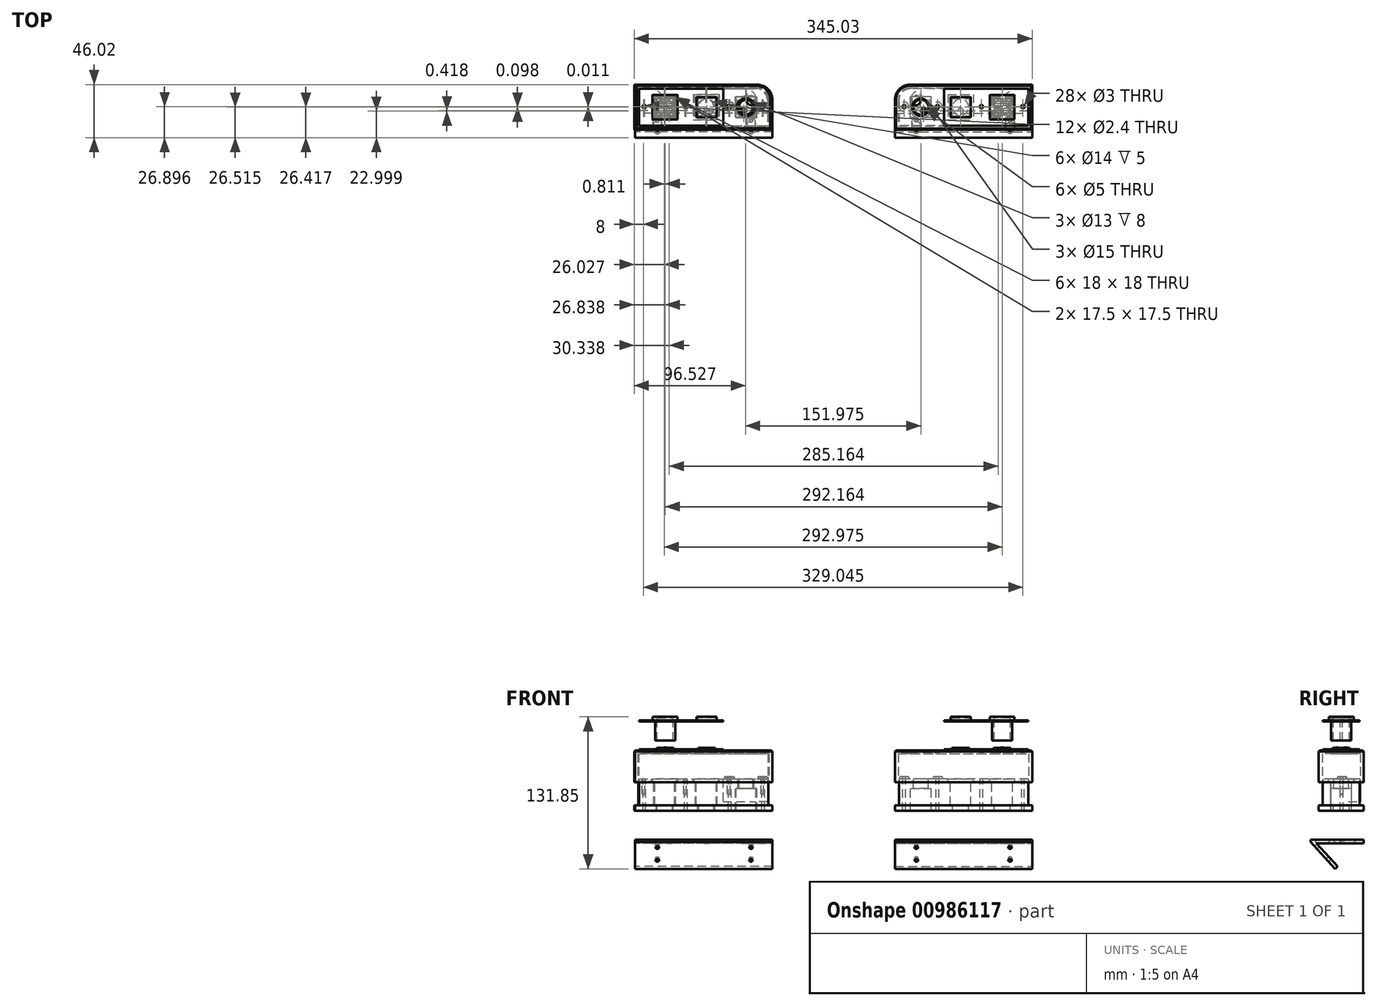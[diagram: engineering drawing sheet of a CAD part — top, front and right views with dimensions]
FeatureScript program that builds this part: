
annotation { "Feature Type Name" : "Feature", "Feature Type Description" : "" }
export const myFeature = defineFeature(function(context is Context, id is Id, definition is map)
    precondition{}
    {
        {
            var Q0;
            Q0=qCreatedBy(makeId("Top.planeOp"),FACE);
            var sketch = newSketch(context, id + "F0", { "sketchPlane" : qUnion([Q0])});
            skLineSegment(sketch, "E0.bottom", {"start": v(66.11, 78.9) * mm, "end": v(169.11, 78.9) * mm});
            skLineSegment(sketch, "E0.top", {"start": v(56.11, 45.9) * mm, "end": v(169.11, 45.9) * mm});
            skLineSegment(sketch, "E0.left", {"start": v(56.11, 68.9) * mm, "end": v(56.11, 45.9) * mm});
            skLineSegment(sketch, "E0.right", {"start": v(169.11, 78.9) * mm, "end": v(169.11, 45.9) * mm});
            skLineSegment(sketch, "E1.bottom", {"start": v(-169.92, 79) * mm, "end": v(-66.92, 79) * mm});
            skLineSegment(sketch, "E1.top", {"start": v(-169.92, 46) * mm, "end": v(-56.92, 46) * mm});
            skLineSegment(sketch, "E1.left", {"start": v(-169.92, 79) * mm, "end": v(-169.92, 46) * mm});
            skLineSegment(sketch, "E1.right", {"start": v(-56.92, 69) * mm, "end": v(-56.92, 46) * mm});
            skPoint(sketch, "E2.visualSharp", {"position": v(-56.92, 79) * mm});
            skArc(sketch, "E2.filletArc", {"start": v(-56.92, 69) * mm, "mid": v(-59.85, 76.07) * mm, "end": v(-66.92, 79) * mm});
            skPoint(sketch, "E3.visualSharp", {"position": v(56.11, 78.9) * mm});
            skArc(sketch, "E3.filletArc", {"start": v(66.11, 78.9) * mm, "mid": v(59.04, 75.97) * mm, "end": v(56.11, 68.9) * mm});
            skSolve(sketch);
        }
        {
            var Q0;
            Q0=qSketchRegion(id+"F0",true);
            extrude(context, id + "F1", {"entities" : qUnion([Q0]), "depth" : 5 * mm, "hasSecondDirection" : true, "secondDirectionOppositeDirection" : true, "secondDirectionDepth" : 19.6 * mm, "offsetDistance" : 25 * mm});
        }
        {
            var Q0;
            Q0=makeQuery(id+"F1.opExtrude","CAP_FACE",FACE,{"disambiguationData":[OSD([sQuery(id+"F0.wireOp",EDGE,"E0.bottom"),sQuery(id+"F0.wireOp",EDGE,"E0.top"),sQuery(id+"F0.wireOp",EDGE,"E0.left"),sQuery(id+"F0.wireOp",EDGE,"E0.right"),sQuery(id+"F0.wireOp",EDGE,"E3.filletArc")])],"isStart":true});
            var Q1;
            Q1=makeQuery(id+"F1.opExtrude","CAP_FACE",FACE,{"disambiguationData":[OSD([sQuery(id+"F0.wireOp",EDGE,"E1.bottom"),sQuery(id+"F0.wireOp",EDGE,"E1.top"),sQuery(id+"F0.wireOp",EDGE,"E1.left"),sQuery(id+"F0.wireOp",EDGE,"E1.right"),sQuery(id+"F0.wireOp",EDGE,"E2.filletArc")])],"isStart":true});
            shell(context, id + "F2", {"entities" : qUnion([Q0, Q1]), "thickness" : 3 * mm, "oppositeDirection" : true});
        }
        {
            var Q0;
            Q0=makeQuery(id+"F1.opExtrude","CAP_FACE",FACE,{"disambiguationData":[OSD([sQuery(id+"F0.wireOp",EDGE,"E0.bottom"),sQuery(id+"F0.wireOp",EDGE,"E0.top"),sQuery(id+"F0.wireOp",EDGE,"E0.left"),sQuery(id+"F0.wireOp",EDGE,"E0.right"),sQuery(id+"F0.wireOp",EDGE,"E3.filletArc")])],"isStart":false});
            cPlane(context, id + "F3", {"entities" : qUnion([Q0]), "cplaneType" : CPlaneType.OFFSET, "offset" : 25 * mm, "width" : 150 * mm, "height" : 150 * mm});
        }
        {
            var Q0;
            Q0=qCreatedBy(id+"F3.planeOp",FACE);
            var sketch = newSketch(context, id + "F4", { "sketchPlane" : qUnion([Q0])});
            skLineSegment(sketch, "E4.bottom", {"start": v(-155.9, 71.5) * mm, "end": v(-137.9, 71.5) * mm});
            skLineSegment(sketch, "E4.top", {"start": v(-155.9, 53.5) * mm, "end": v(-137.9, 53.5) * mm});
            skLineSegment(sketch, "E4.left", {"start": v(-155.9, 71.5) * mm, "end": v(-155.9, 53.5) * mm});
            skLineSegment(sketch, "E4.right", {"start": v(-137.9, 71.5) * mm, "end": v(-137.9, 53.5) * mm});
            skLineSegment(sketch, "E5.bottom", {"start": v(-119.9, 71.5) * mm, "end": v(-101.9, 71.5) * mm});
            skLineSegment(sketch, "E5.top", {"start": v(-119.9, 53.5) * mm, "end": v(-101.9, 53.5) * mm});
            skLineSegment(sketch, "E5.left", {"start": v(-119.9, 71.5) * mm, "end": v(-119.9, 53.5) * mm});
            skLineSegment(sketch, "E5.right", {"start": v(-101.9, 71.5) * mm, "end": v(-101.9, 53.5) * mm});
            skCircle(sketch, "E6", {"center": v(-76.4, 62.5) * mm, "radius": 7.5 * mm});
            skCircle(sketch, "E7", {"center": v(75.58, 62.4) * mm, "radius": 7.5 * mm});
            skLineSegment(sketch, "E8.bottom", {"start": v(101.08, 71.4) * mm, "end": v(119.08, 71.4) * mm});
            skLineSegment(sketch, "E8.top", {"start": v(101.08, 53.4) * mm, "end": v(119.08, 53.4) * mm});
            skLineSegment(sketch, "E8.left", {"start": v(101.08, 71.4) * mm, "end": v(101.08, 53.4) * mm});
            skLineSegment(sketch, "E8.right", {"start": v(119.08, 71.4) * mm, "end": v(119.08, 53.4) * mm});
            skLineSegment(sketch, "E9.bottom", {"start": v(137.08, 71.4) * mm, "end": v(155.08, 71.4) * mm});
            skLineSegment(sketch, "E9.top", {"start": v(137.08, 53.4) * mm, "end": v(155.08, 53.4) * mm});
            skLineSegment(sketch, "E9.left", {"start": v(137.08, 71.4) * mm, "end": v(137.08, 53.4) * mm});
            skLineSegment(sketch, "E9.right", {"start": v(155.08, 71.4) * mm, "end": v(155.08, 53.4) * mm});
            skSolve(sketch);
        }
        {
            var Q0;
            Q0=qSketchRegion(id+"F4",true);
            extrude(context, id + "F5", {"entities" : qUnion([Q0]), "operationType" : NewBodyOperationType.REMOVE, "oppositeDirection" : true, "depth" : 50 * mm});
        }
        {
            var Q0;
            Q0=makeQuery(id+"F1.opExtrude","CAP_FACE",FACE,{"disambiguationData":[OSD([sQuery(id+"F0.wireOp",EDGE,"E1.bottom"),sQuery(id+"F0.wireOp",EDGE,"E1.top"),sQuery(id+"F0.wireOp",EDGE,"E1.left"),sQuery(id+"F0.wireOp",EDGE,"E1.right"),sQuery(id+"F0.wireOp",EDGE,"E2.filletArc")])],"isStart":false});
            cPlane(context, id + "F6", {"entities" : qUnion([Q0]), "cplaneType" : CPlaneType.OFFSET, "offset" : 0 * mm, "width" : 150 * mm, "height" : 150 * mm});
        }
        {
            var Q0;
            Q0=qCreatedBy(id+"F6.planeOp",FACE);
            var sketch = newSketch(context, id + "F7", { "sketchPlane" : qUnion([Q0])});
            skPoint(sketch, "E10", {"position": v(-164.92, 62.89) * mm});
            skPoint(sketch, "E11", {"position": v(-128.9, 62.89) * mm});
            skPoint(sketch, "E12", {"position": v(-90.9, 62.89) * mm});
            skPoint(sketch, "E13", {"position": v(-61.92, 62.89) * mm});
            skPoint(sketch, "E14", {"position": v(61.11, 62.89) * mm});
            skPoint(sketch, "E15", {"position": v(90.08, 62.89) * mm});
            skPoint(sketch, "E16", {"position": v(128.08, 62.89) * mm});
            skPoint(sketch, "E17", {"position": v(164.11, 62.89) * mm});
            skSolve(sketch);
        }
        {
            var Q0;
            Q0=sQuery(id+"F7.wireOp",VERTEX,"E11");
            var Q1;
            Q1=sQuery(id+"F7.wireOp",VERTEX,"E17");
            var Q2;
            Q2=sQuery(id+"F7.wireOp",VERTEX,"E16");
            var Q3;
            Q3=sQuery(id+"F7.wireOp",VERTEX,"E10");
            var Q4;
            Q4=sQuery(id+"F7.wireOp",VERTEX,"E15");
            var Q5;
            Q5=sQuery(id+"F7.wireOp",VERTEX,"E14");
            var Q6;
            Q6=sQuery(id+"F7.wireOp",VERTEX,"E12");
            var Q7;
            Q7=sQuery(id+"F7.wireOp",VERTEX,"E13");
            var Q8;
            Q8=makeQuery(id+"F1.opExtrude","SWEPT_BODY",BODY,{"disambiguationData":[OSD([sQuery(id+"F0.wireOp",EDGE,"E0.bottom"),sQuery(id+"F0.wireOp",EDGE,"E0.top"),sQuery(id+"F0.wireOp",EDGE,"E0.left"),sQuery(id+"F0.wireOp",EDGE,"E0.right"),sQuery(id+"F0.wireOp",EDGE,"E3.filletArc")])]});
            var Q9;
            Q9=makeQuery(id+"F1.opExtrude","SWEPT_BODY",BODY,{"disambiguationData":[OSD([sQuery(id+"F0.wireOp",EDGE,"E1.bottom"),sQuery(id+"F0.wireOp",EDGE,"E1.top"),sQuery(id+"F0.wireOp",EDGE,"E1.left"),sQuery(id+"F0.wireOp",EDGE,"E1.right"),sQuery(id+"F0.wireOp",EDGE,"E2.filletArc")])]});
            hole(context, id + "F8", {"style" : HoleStyle.SIMPLE, "endStyle" : HoleEndStyle.BLIND, "holeDiameter" : 3 * mm, "holeDepth" : 40 * mm, "startFromSketch" : true, "locations" : qUnion([Q0, Q1, Q2, Q3, Q4, Q5, Q6, Q7]), "scope" : qUnion([Q8, Q9])});
        }
        {
            var Q0;
            Q0=makeQuery(id+"F1.opExtrude","CAP_EDGE",EDGE,{"disambiguationData":[OSD([sQuery(id+"F0.wireOp",EDGE,"E1.top")])],"isStart":false});
            var Q1;
            Q1=makeQuery(id+"F1.opExtrude","CAP_EDGE",EDGE,{"disambiguationData":[OSD([sQuery(id+"F0.wireOp",EDGE,"E1.left")])],"isStart":false});
            var Q2;
            Q2=makeQuery(id+"F1.opExtrude","CAP_EDGE",EDGE,{"disambiguationData":[OSD([sQuery(id+"F0.wireOp",EDGE,"E1.bottom")])],"isStart":false});
            var Q3;
            Q3=makeQuery(id+"F1.opExtrude","CAP_EDGE",EDGE,{"disambiguationData":[OSD([sQuery(id+"F0.wireOp",EDGE,"E0.left")])],"isStart":false});
            var Q4;
            Q4=makeQuery(id+"F1.opExtrude","CAP_EDGE",EDGE,{"disambiguationData":[OSD([sQuery(id+"F0.wireOp",EDGE,"E0.top")])],"isStart":false});
            var Q5;
            Q5=makeQuery(id+"F1.opExtrude","CAP_EDGE",EDGE,{"disambiguationData":[OSD([sQuery(id+"F0.wireOp",EDGE,"E0.right")])],"isStart":false});
            chamfer(context, id + "F9", {"entities" : qUnion([Q0, Q1, Q2, Q3, Q4, Q5]), "width" : 1 * mm, "tangentPropagation" : true});
        }
        {
            var Q0;
            Q0=makeQuery(id+"F1.opExtrude","CAP_FACE",FACE,{"disambiguationData":[OSD([sQuery(id+"F0.wireOp",EDGE,"E0.bottom"),sQuery(id+"F0.wireOp",EDGE,"E0.top"),sQuery(id+"F0.wireOp",EDGE,"E0.left"),sQuery(id+"F0.wireOp",EDGE,"E0.right"),sQuery(id+"F0.wireOp",EDGE,"E3.filletArc")])],"isStart":true});
            cPlane(context, id + "F10", {"entities" : qUnion([Q0]), "cplaneType" : CPlaneType.OFFSET, "offset" : 25 * mm, "width" : 150 * mm, "height" : 150 * mm});
        }
        {
            var Q0;
            Q0=qCreatedBy(id+"F10.planeOp",FACE);
            var sketch = newSketch(context, id + "F11", { "sketchPlane" : qUnion([Q0])});
            skLineSegment(sketch, "E18.bottom", {"start": v(53.11, -42.9) * mm, "end": v(172.11, -42.9) * mm});
            skLineSegment(sketch, "E18.top", {"start": v(66.11, -81.9) * mm, "end": v(172.11, -81.9) * mm});
            skLineSegment(sketch, "E18.left", {"start": v(53.11, -42.9) * mm, "end": v(53.11, -68.9) * mm});
            skLineSegment(sketch, "E18.right", {"start": v(172.11, -42.9) * mm, "end": v(172.11, -81.9) * mm});
            skLineSegment(sketch, "E19.bottom", {"start": v(-172.92, -43) * mm, "end": v(-53.92, -43) * mm});
            skLineSegment(sketch, "E19.top", {"start": v(-172.92, -81.9) * mm, "end": v(-66.92, -81.9) * mm});
            skLineSegment(sketch, "E19.left", {"start": v(-172.92, -43) * mm, "end": v(-172.92, -81.9) * mm});
            skLineSegment(sketch, "E19.right", {"start": v(-53.92, -43) * mm, "end": v(-53.92, -68.9) * mm});
            skPoint(sketch, "E20.visualSharp", {"position": v(53.11, -81.9) * mm});
            skArc(sketch, "E20.filletArc", {"start": v(53.11, -68.9) * mm, "mid": v(56.92, -78.09) * mm, "end": v(66.11, -81.9) * mm});
            skPoint(sketch, "E21.visualSharp", {"position": v(-53.92, -81.9) * mm});
            skArc(sketch, "E21.filletArc", {"start": v(-66.92, -81.9) * mm, "mid": v(-57.73, -78.09) * mm, "end": v(-53.92, -68.9) * mm});
            skSolve(sketch);
        }
        {
            var Q0;
            Q0=qSketchRegion(id+"F11",true);
            extrude(context, id + "F12", {"entities" : qUnion([Q0]), "oppositeDirection" : true, "depth" : 5 * mm, "offsetDistance" : 25 * mm});
        }
        {
            var Q0;
            Q0=makeQuery(id+"F12.opExtrude","CAP_FACE",FACE,{"disambiguationData":[OSD([sQuery(id+"F11.wireOp",EDGE,"E18.bottom"),sQuery(id+"F11.wireOp",EDGE,"E18.top"),sQuery(id+"F11.wireOp",EDGE,"E18.left"),sQuery(id+"F11.wireOp",EDGE,"E18.right"),sQuery(id+"F11.wireOp",EDGE,"E20.filletArc")])],"isStart":false});
            cPlane(context, id + "F13", {"entities" : qUnion([Q0]), "cplaneType" : CPlaneType.OFFSET, "offset" : 25 * mm, "width" : 150 * mm, "height" : 150 * mm});
        }
        {
            var Q0;
            Q0=makeQuery(id+"F12.opExtrude","CAP_FACE",FACE,{"disambiguationData":[OSD([sQuery(id+"F11.wireOp",EDGE,"E18.bottom"),sQuery(id+"F11.wireOp",EDGE,"E18.top"),sQuery(id+"F11.wireOp",EDGE,"E18.left"),sQuery(id+"F11.wireOp",EDGE,"E18.right"),sQuery(id+"F11.wireOp",EDGE,"E20.filletArc")])],"isStart":false});
            cPlane(context, id + "F14", {"entities" : qUnion([Q0]), "cplaneType" : CPlaneType.OFFSET, "offset" : 0 * mm, "width" : 150 * mm, "height" : 150 * mm});
        }
        {
            var Q0;
            Q0=qCreatedBy(id+"F14.planeOp",FACE);
            var sketch = newSketch(context, id + "F15", { "sketchPlane" : qUnion([Q0])});
            skLineSegment(sketch, "E22.bottom", {"start": v(66.61, 78.4) * mm, "end": v(168.61, 78.4) * mm});
            skLineSegment(sketch, "E22.top", {"start": v(56.61, 46.4) * mm, "end": v(168.61, 46.4) * mm});
            skLineSegment(sketch, "E22.left", {"start": v(56.61, 68.4) * mm, "end": v(56.61, 46.4) * mm});
            skLineSegment(sketch, "E22.right", {"start": v(168.61, 78.4) * mm, "end": v(168.61, 46.4) * mm});
            skPoint(sketch, "E23.oppositeSnap0", {"position": v(112.61, 46.4) * mm});
            skPoint(sketch, "E24.visualSharp", {"position": v(56.61, 78.4) * mm});
            skArc(sketch, "E24.filletArc", {"start": v(66.61, 78.4) * mm, "mid": v(59.54, 75.47) * mm, "end": v(56.61, 68.4) * mm});
            skSolve(sketch);
        }
        {
            var Q0;
            Q0=qSketchRegion(id+"F15",true);
            extrude(context, id + "F16", {"entities" : qUnion([Q0]), "operationType" : NewBodyOperationType.ADD, "depth" : 3 * mm, "offsetDistance" : 25 * mm});
        }
        {
            var Q0;
            Q0=qCreatedBy(id+"F14.planeOp",FACE);
            var sketch = newSketch(context, id + "F17", { "sketchPlane" : qUnion([Q0])});
            skLineSegment(sketch, "E25.bottom", {"start": v(-169.42, 78.5) * mm, "end": v(-67.42, 78.5) * mm});
            skLineSegment(sketch, "E25.top", {"start": v(-169.42, 46.5) * mm, "end": v(-57.42, 46.5) * mm});
            skLineSegment(sketch, "E25.left", {"start": v(-169.42, 78.5) * mm, "end": v(-169.42, 46.5) * mm});
            skLineSegment(sketch, "E25.right", {"start": v(-57.42, 68.5) * mm, "end": v(-57.42, 46.5) * mm});
            skPoint(sketch, "E26.visualSharp", {"position": v(-57.42, 78.5) * mm});
            skArc(sketch, "E26.filletArc", {"start": v(-57.42, 68.5) * mm, "mid": v(-60.35, 75.57) * mm, "end": v(-67.42, 78.5) * mm});
            skSolve(sketch);
        }
        {
            var Q0;
            Q0=qSketchRegion(id+"F17",true);
            extrude(context, id + "F18", {"entities" : qUnion([Q0]), "operationType" : NewBodyOperationType.ADD, "depth" : 3 * mm, "offsetDistance" : 25 * mm});
        }
        {
            var Q0;
            Q0=makeQuery(id+"F16.opExtrude","CAP_FACE",FACE,{"disambiguationData":[OSD([sQuery(id+"F15.wireOp",EDGE,"E22.bottom"),sQuery(id+"F15.wireOp",EDGE,"E22.top"),sQuery(id+"F15.wireOp",EDGE,"E22.left"),sQuery(id+"F15.wireOp",EDGE,"E22.right"),sQuery(id+"F15.wireOp",EDGE,"E24.filletArc")])],"isStart":false});
            cPlane(context, id + "F19", {"entities" : qUnion([Q0]), "cplaneType" : CPlaneType.OFFSET, "offset" : 0 * mm, "width" : 150 * mm, "height" : 150 * mm});
        }
        {
            var Q0;
            Q0=qCreatedBy(id+"F19.planeOp",FACE);
            var sketch = newSketch(context, id + "F20", { "sketchPlane" : qUnion([Q0])});
            skLineSegment(sketch, "E27.bottom", {"start": v(95.11, 78.4) * mm, "end": v(66.61, 78.4) * mm});
            skLineSegment(sketch, "E27.top", {"start": v(95.11, 46.4) * mm, "end": v(56.61, 46.4) * mm});
            skLineSegment(sketch, "E27.left", {"start": v(95.11, 78.4) * mm, "end": v(95.11, 46.4) * mm});
            skLineSegment(sketch, "E27.right", {"start": v(56.61, 68.4) * mm, "end": v(56.61, 46.4) * mm});
            skPoint(sketch, "E28.visualSharp", {"position": v(56.61, 78.4) * mm});
            skArc(sketch, "E28.filletArc", {"start": v(66.61, 78.4) * mm, "mid": v(59.54, 75.47) * mm, "end": v(56.61, 68.4) * mm});
            skSolve(sketch);
        }
        {
            var Q0;
            Q0=qSketchRegion(id+"F20",true);
            extrude(context, id + "F21", {"entities" : qUnion([Q0]), "operationType" : NewBodyOperationType.ADD, "depth" : 19.6 * mm, "offsetDistance" : 25 * mm});
        }
        {
            var Q0;
            Q0=makeQuery(id+"F5.boolean.opBoolean","INTERSECT",EDGE,{"derivedFrom":[makeQuery(id+"F2.opShell","OFFSET_FACE",FACE,{"disambiguationData":[OSD([sQuery(id+"F0.wireOp",EDGE,"E1.bottom"),sQuery(id+"F0.wireOp",EDGE,"E1.top"),sQuery(id+"F0.wireOp",EDGE,"E1.left"),sQuery(id+"F0.wireOp",EDGE,"E1.right"),sQuery(id+"F0.wireOp",EDGE,"E2.filletArc")])]}),makeQuery(id+"F5.opExtrude","SWEPT_FACE",FACE,{"disambiguationData":[OSD([sQuery(id+"F4.wireOp",EDGE,"E6")])]})]});
            var Q1;
            Q1=makeQuery(id+"F5.boolean.opBoolean","INTERSECT",EDGE,{"derivedFrom":[makeQuery(id+"F2.opShell","OFFSET_FACE",FACE,{"disambiguationData":[OSD([sQuery(id+"F0.wireOp",EDGE,"E0.bottom"),sQuery(id+"F0.wireOp",EDGE,"E0.top"),sQuery(id+"F0.wireOp",EDGE,"E0.left"),sQuery(id+"F0.wireOp",EDGE,"E0.right"),sQuery(id+"F0.wireOp",EDGE,"E3.filletArc")])]}),makeQuery(id+"F5.opExtrude","SWEPT_FACE",FACE,{"disambiguationData":[OSD([sQuery(id+"F4.wireOp",EDGE,"E7")])]})]});
            chamfer(context, id + "F22", {"entities" : qUnion([Q0, Q1]), "width" : 2 * mm, "tangentPropagation" : true});
        }
        {
            var Q0;
            Q0=qCreatedBy(id+"F19.planeOp",FACE);
            var sketch = newSketch(context, id + "F23", { "sketchPlane" : qUnion([Q0])});
            skLineSegment(sketch, "E29.bottom", {"start": v(-95.92, 78.6) * mm, "end": v(-67.42, 78.6) * mm});
            skLineSegment(sketch, "E29.top", {"start": v(-95.92, 46.5) * mm, "end": v(-57.42, 46.5) * mm});
            skLineSegment(sketch, "E29.left", {"start": v(-95.92, 78.6) * mm, "end": v(-95.92, 46.5) * mm});
            skLineSegment(sketch, "E29.right", {"start": v(-57.42, 68.6) * mm, "end": v(-57.42, 46.5) * mm});
            skPoint(sketch, "E30.visualSharp", {"position": v(-57.42, 78.6) * mm});
            skArc(sketch, "E30.filletArc", {"start": v(-57.42, 68.6) * mm, "mid": v(-60.35, 75.66) * mm, "end": v(-67.42, 78.6) * mm});
            skSolve(sketch);
        }
        {
            var Q0;
            Q0=qSketchRegion(id+"F23",true);
            extrude(context, id + "F24", {"entities" : qUnion([Q0]), "operationType" : NewBodyOperationType.ADD, "depth" : 19.6 * mm, "offsetDistance" : 25 * mm});
        }
        {
            var Q0;
            Q0=makeQuery(id+"F21.opExtrude","CAP_FACE",FACE,{"disambiguationData":[OSD([sQuery(id+"F20.wireOp",EDGE,"E27.bottom"),sQuery(id+"F20.wireOp",EDGE,"E27.top"),sQuery(id+"F20.wireOp",EDGE,"E27.left"),sQuery(id+"F20.wireOp",EDGE,"E27.right"),sQuery(id+"F20.wireOp",EDGE,"E28.filletArc")])],"isStart":false});
            cPlane(context, id + "F25", {"entities" : qUnion([Q0]), "cplaneType" : CPlaneType.OFFSET, "offset" : 0 * mm, "width" : 150 * mm, "height" : 150 * mm});
        }
        {
            var Q0;
            Q0=qCreatedBy(id+"F25.planeOp",FACE);
            var sketch = newSketch(context, id + "F26", { "sketchPlane" : qUnion([Q0])});
            skCircle(sketch, "E31", {"center": v(75.58, 62.4) * mm, "radius": 6.5 * mm});
            skCircle(sketch, "E32", {"center": v(-76.4, 62.5) * mm, "radius": 6.5 * mm});
            skSolve(sketch);
        }
        {
            var Q0;
            Q0=qSketchRegion(id+"F26",true);
            extrude(context, id + "F27", {"entities" : qUnion([Q0]), "operationType" : NewBodyOperationType.REMOVE, "oppositeDirection" : true, "depth" : 8 * mm, "offsetDistance" : 25 * mm});
        }
        {
            var Q0;
            Q0=makeQuery(id+"F27.boolean.opBoolean","COPY",FACE,{"derivedFrom":makeQuery(id+"F27.opExtrude","CAP_FACE",FACE,{"disambiguationData":[OSD([sQuery(id+"F26.wireOp",EDGE,"E31")])],"isStart":false})});
            var sketch = newSketch(context, id + "F28", { "sketchPlane" : qUnion([Q0])});
            skLineSegment(sketch, "E33.bottom", {"start": v(66.58, 71.4) * mm, "end": v(84.58, 71.4) * mm});
            skLineSegment(sketch, "E33.top", {"start": v(66.58, 53.4) * mm, "end": v(84.58, 53.4) * mm});
            skLineSegment(sketch, "E33.left", {"start": v(66.58, 71.4) * mm, "end": v(66.58, 53.4) * mm});
            skLineSegment(sketch, "E33.right", {"start": v(84.58, 71.4) * mm, "end": v(84.58, 53.4) * mm});
            skSolve(sketch);
        }
        {
            var Q0;
            Q0=qSketchRegion(id+"F28",true);
            extrude(context, id + "F29", {"entities" : qUnion([Q0]), "operationType" : NewBodyOperationType.REMOVE, "oppositeDirection" : true, "depth" : 25 * mm, "offsetDistance" : 25 * mm});
        }
        {
            var Q0;
            Q0=makeQuery(id+"F27.boolean.opBoolean","COPY",FACE,{"derivedFrom":makeQuery(id+"F27.opExtrude","CAP_FACE",FACE,{"disambiguationData":[OSD([sQuery(id+"F26.wireOp",EDGE,"E32")])],"isStart":false})});
            var sketch = newSketch(context, id + "F30", { "sketchPlane" : qUnion([Q0])});
            skLineSegment(sketch, "E34.bottom", {"start": v(-85.4, 71.5) * mm, "end": v(-67.4, 71.5) * mm});
            skLineSegment(sketch, "E34.top", {"start": v(-85.4, 53.5) * mm, "end": v(-67.4, 53.5) * mm});
            skLineSegment(sketch, "E34.left", {"start": v(-85.4, 71.5) * mm, "end": v(-85.4, 53.5) * mm});
            skLineSegment(sketch, "E34.right", {"start": v(-67.4, 71.5) * mm, "end": v(-67.4, 53.5) * mm});
            skSolve(sketch);
        }
        {
            var Q0;
            Q0=qSketchRegion(id+"F30",true);
            extrude(context, id + "F31", {"entities" : qUnion([Q0]), "operationType" : NewBodyOperationType.REMOVE, "oppositeDirection" : true, "depth" : 25 * mm, "offsetDistance" : 25 * mm});
        }
        {
            var Q0;
            Q0=qCreatedBy(id+"F13.planeOp",FACE);
            var sketch = newSketch(context, id + "F32", { "sketchPlane" : qUnion([Q0])});
            skPoint(sketch, "E35", {"position": v(61.11, 62.89) * mm});
            skPoint(sketch, "E36", {"position": v(90.08, 62.89) * mm});
            skSolve(sketch);
        }
        {
            var Q0;
            Q0=qCreatedBy(id+"F13.planeOp",FACE);
            var sketch = newSketch(context, id + "F33", { "sketchPlane" : qUnion([Q0])});
            skPoint(sketch, "E37", {"position": v(-90.9, 62.89) * mm});
            skPoint(sketch, "E38", {"position": v(-61.92, 62.89) * mm});
            skSolve(sketch);
        }
        {
            var Q0;
            Q0=qCreatedBy(id+"F25.planeOp",FACE);
            var sketch = newSketch(context, id + "F34", { "sketchPlane" : qUnion([Q0])});
            skCircle(sketch, "E39", {"center": v(90.08, 62.89) * mm, "radius": 4 * mm});
            skCircle(sketch, "E40", {"center": v(61.11, 62.89) * mm, "radius": 4 * mm});
            skSolve(sketch);
        }
        {
            var Q0;
            Q0=qCreatedBy(id+"F25.planeOp",FACE);
            var sketch = newSketch(context, id + "F35", { "sketchPlane" : qUnion([Q0])});
            skCircle(sketch, "E41", {"center": v(-61.92, 62.89) * mm, "radius": 4 * mm});
            skCircle(sketch, "E42", {"center": v(-90.9, 62.89) * mm, "radius": 4 * mm});
            skSolve(sketch);
        }
        {
            var Q0;
            Q0=qSketchRegion(id+"F34",true);
            extrude(context, id + "F36", {"entities" : qUnion([Q0]), "operationType" : NewBodyOperationType.ADD, "depth" : 2 * mm, "offsetDistance" : 25 * mm});
        }
        {
            var Q0;
            Q0=qSketchRegion(id+"F35",true);
            extrude(context, id + "F37", {"entities" : qUnion([Q0]), "operationType" : NewBodyOperationType.ADD, "depth" : 2 * mm, "offsetDistance" : 25 * mm});
        }
        {
            var Q0;
            Q0=sQuery(id+"F32.wireOp",VERTEX,"E35");
            var Q1;
            Q1=sQuery(id+"F32.wireOp",VERTEX,"E36");
            var Q2;
            Q2=sQuery(id+"F33.wireOp",VERTEX,"E37");
            var Q3;
            Q3=sQuery(id+"F33.wireOp",VERTEX,"E38");
            var Q4;
            Q4=makeQuery(id+"F12.opExtrude","SWEPT_BODY",BODY,{"disambiguationData":[OSD([sQuery(id+"F11.wireOp",EDGE,"E18.bottom"),sQuery(id+"F11.wireOp",EDGE,"E18.top"),sQuery(id+"F11.wireOp",EDGE,"E18.left"),sQuery(id+"F11.wireOp",EDGE,"E18.right"),sQuery(id+"F11.wireOp",EDGE,"E20.filletArc")])]});
            var Q5;
            Q5=makeQuery(id+"F12.opExtrude","SWEPT_BODY",BODY,{"disambiguationData":[OSD([sQuery(id+"F11.wireOp",EDGE,"E19.bottom"),sQuery(id+"F11.wireOp",EDGE,"E19.top"),sQuery(id+"F11.wireOp",EDGE,"E19.left"),sQuery(id+"F11.wireOp",EDGE,"E19.right"),sQuery(id+"F11.wireOp",EDGE,"E21.filletArc")])]});
            hole(context, id + "F38", {"style" : HoleStyle.SIMPLE, "endStyle" : HoleEndStyle.BLIND, "holeDiameter" : 2.4 * mm, "holeDepth" : 15 * mm, "tappedDepth" : 12 * mm, "tapClearance" : 3, "locations" : qUnion([Q0, Q1, Q2, Q3]), "scope" : qUnion([Q4, Q5])});
        }
        {
            var Q0;
            Q0=makeQuery(id+"F1.opExtrude","CAP_FACE",FACE,{"disambiguationData":[OSD([sQuery(id+"F0.wireOp",EDGE,"E1.bottom"),sQuery(id+"F0.wireOp",EDGE,"E1.top"),sQuery(id+"F0.wireOp",EDGE,"E1.left"),sQuery(id+"F0.wireOp",EDGE,"E1.right"),sQuery(id+"F0.wireOp",EDGE,"E2.filletArc")])],"isStart":false});
            var sketch = newSketch(context, id + "F39", { "sketchPlane" : qUnion([Q0])});
            skLineSegment(sketch, "E43.bottom", {"start": v(168.63, 78.39) * mm, "end": v(95.63, 78.39) * mm});
            skLineSegment(sketch, "E43.top", {"start": v(168.63, 46.39) * mm, "end": v(95.63, 46.39) * mm});
            skLineSegment(sketch, "E43.left", {"start": v(168.63, 78.39) * mm, "end": v(168.63, 46.39) * mm});
            skLineSegment(sketch, "E43.right", {"start": v(95.63, 78.39) * mm, "end": v(95.63, 46.39) * mm});
            skLineSegment(sketch, "E44.bottom", {"start": v(-169.42, 78.5) * mm, "end": v(-96.42, 78.5) * mm});
            skLineSegment(sketch, "E44.top", {"start": v(-169.42, 46.5) * mm, "end": v(-96.42, 46.5) * mm});
            skLineSegment(sketch, "E44.left", {"start": v(-169.42, 78.5) * mm, "end": v(-169.42, 46.5) * mm});
            skLineSegment(sketch, "E44.right", {"start": v(-96.42, 78.5) * mm, "end": v(-96.42, 46.5) * mm});
            skCircle(sketch, "E45", {"center": v(-164.92, 62.9) * mm, "radius": 1.5 * mm});
            skCircle(sketch, "E46", {"center": v(-128.9, 62.9) * mm, "radius": 1.5 * mm});
            skCircle(sketch, "E47", {"center": v(128.1, 62.88) * mm, "radius": 1.5 * mm});
            skCircle(sketch, "E48", {"center": v(164.13, 62.88) * mm, "radius": 1.5 * mm});
            skSolve(sketch);
        }
        {
            var Q0;
            Q0=qSketchRegion(id+"F39",true);
            extrude(context, id + "F40", {"entities" : qUnion([Q0]), "depth" : 1 * mm, "offsetDistance" : 25 * mm});
        }
        {
            var Q0;
            Q0=makeQuery(id+"F40.opExtrude","CAP_FACE",FACE,{"disambiguationData":[OSD([sQuery(id+"F39.wireOp",EDGE,"E43.bottom"),sQuery(id+"F39.wireOp",EDGE,"E43.top"),sQuery(id+"F39.wireOp",EDGE,"E43.left"),sQuery(id+"F39.wireOp",EDGE,"E43.right"),sQuery(id+"F39.wireOp",EDGE,"E47"),sQuery(id+"F39.wireOp",EDGE,"E48")])],"isStart":false});
            cPlane(context, id + "F41", {"entities" : qUnion([Q0]), "cplaneType" : CPlaneType.OFFSET, "offset" : 25 * mm, "width" : 150 * mm, "height" : 150 * mm});
        }
        {
            var Q0;
            Q0=qCreatedBy(id+"F41.planeOp",FACE);
            var sketch = newSketch(context, id + "F42", { "sketchPlane" : qUnion([Q0])});
            skLineSegment(sketch, "E49.bottom", {"start": v(95.63, 78.39) * mm, "end": v(168.63, 78.39) * mm});
            skLineSegment(sketch, "E49.top", {"start": v(95.63, 46.39) * mm, "end": v(168.63, 46.39) * mm});
            skLineSegment(sketch, "E49.left", {"start": v(95.63, 78.39) * mm, "end": v(95.63, 46.39) * mm});
            skLineSegment(sketch, "E49.right", {"start": v(168.63, 78.39) * mm, "end": v(168.63, 46.39) * mm});
            skCircle(sketch, "E50", {"center": v(128.1, 62.88) * mm, "radius": 1.5 * mm});
            skCircle(sketch, "E51", {"center": v(164.13, 62.88) * mm, "radius": 1.5 * mm});
            skSolve(sketch);
        }
        {
            var Q0;
            Q0=qSketchRegion(id+"F42",true);
            extrude(context, id + "F43", {"entities" : qUnion([Q0]), "oppositeDirection" : true, "depth" : 1 * mm, "offsetDistance" : 25 * mm});
        }
        {
            var Q0;
            Q0=makeQuery(id+"F43.opExtrude","CAP_FACE",FACE,{"disambiguationData":[OSD([sQuery(id+"F42.wireOp",EDGE,"E49.bottom"),sQuery(id+"F42.wireOp",EDGE,"E49.top"),sQuery(id+"F42.wireOp",EDGE,"E49.left"),sQuery(id+"F42.wireOp",EDGE,"E49.right"),sQuery(id+"F42.wireOp",EDGE,"E50"),sQuery(id+"F42.wireOp",EDGE,"E51")])],"isStart":true});
            var sketch = newSketch(context, id + "F44", { "sketchPlane" : qUnion([Q0])});
            skLineSegment(sketch, "E52.bottom", {"start": v(101.33, 71.15) * mm, "end": v(118.83, 71.15) * mm});
            skLineSegment(sketch, "E52.top", {"start": v(101.33, 53.65) * mm, "end": v(118.83, 53.65) * mm});
            skLineSegment(sketch, "E52.left", {"start": v(101.33, 71.15) * mm, "end": v(101.33, 53.65) * mm});
            skLineSegment(sketch, "E52.right", {"start": v(118.83, 71.15) * mm, "end": v(118.83, 53.65) * mm});
            skLineSegment(sketch, "E53.bottom", {"start": v(137.33, 71.15) * mm, "end": v(154.83, 71.15) * mm});
            skLineSegment(sketch, "E53.top", {"start": v(137.33, 53.65) * mm, "end": v(154.83, 53.65) * mm});
            skLineSegment(sketch, "E53.left", {"start": v(137.33, 71.15) * mm, "end": v(137.33, 53.65) * mm});
            skLineSegment(sketch, "E53.right", {"start": v(154.83, 71.15) * mm, "end": v(154.83, 53.65) * mm});
            skSolve(sketch);
        }
        {
            var Q0;
            Q0=qSketchRegion(id+"F44",true);
            extrude(context, id + "F45", {"entities" : qUnion([Q0]), "operationType" : NewBodyOperationType.ADD, "depth" : 3 * mm, "offsetDistance" : 25 * mm});
        }
        {
            var Q0;
            Q0=makeQuery(id+"F43.opExtrude","CAP_FACE",FACE,{"disambiguationData":[OSD([sQuery(id+"F42.wireOp",EDGE,"E49.bottom"),sQuery(id+"F42.wireOp",EDGE,"E49.top"),sQuery(id+"F42.wireOp",EDGE,"E49.left"),sQuery(id+"F42.wireOp",EDGE,"E49.right"),sQuery(id+"F42.wireOp",EDGE,"E50"),sQuery(id+"F42.wireOp",EDGE,"E51")])],"isStart":false});
            var sketch = newSketch(context, id + "F46", { "sketchPlane" : qUnion([Q0])});
            skLineSegment(sketch, "E54.bottom", {"start": v(102.33, -70.15) * mm, "end": v(117.83, -70.15) * mm});
            skLineSegment(sketch, "E54.top", {"start": v(102.33, -54.65) * mm, "end": v(117.83, -54.65) * mm});
            skLineSegment(sketch, "E54.left", {"start": v(102.33, -70.15) * mm, "end": v(102.33, -54.65) * mm});
            skLineSegment(sketch, "E54.right", {"start": v(117.83, -70.15) * mm, "end": v(117.83, -54.65) * mm});
            skLineSegment(sketch, "E55.bottom", {"start": v(138.33, -70.15) * mm, "end": v(153.83, -70.15) * mm});
            skLineSegment(sketch, "E55.top", {"start": v(138.33, -54.65) * mm, "end": v(153.83, -54.65) * mm});
            skLineSegment(sketch, "E55.left", {"start": v(138.33, -70.15) * mm, "end": v(138.33, -54.65) * mm});
            skLineSegment(sketch, "E55.right", {"start": v(153.83, -70.15) * mm, "end": v(153.83, -54.65) * mm});
            skSolve(sketch);
        }
        {
            var Q0;
            Q0=qSketchRegion(id+"F46",true);
            extrude(context, id + "F47", {"entities" : qUnion([Q0]), "operationType" : NewBodyOperationType.REMOVE, "oppositeDirection" : true, "depth" : 3 * mm, "offsetDistance" : 25 * mm});
        }
        {
            var Q0;
            Q0=makeQuery(id+"F40.opExtrude","CAP_FACE",FACE,{"disambiguationData":[OSD([sQuery(id+"F39.wireOp",EDGE,"E43.bottom"),sQuery(id+"F39.wireOp",EDGE,"E43.top"),sQuery(id+"F39.wireOp",EDGE,"E43.left"),sQuery(id+"F39.wireOp",EDGE,"E43.right"),sQuery(id+"F39.wireOp",EDGE,"E47"),sQuery(id+"F39.wireOp",EDGE,"E48")])],"isStart":false});
            var sketch = newSketch(context, id + "F48", { "sketchPlane" : qUnion([Q0])});
            skLineSegment(sketch, "E56.bottom", {"start": v(102.58, 69.9) * mm, "end": v(117.58, 69.9) * mm});
            skLineSegment(sketch, "E56.top", {"start": v(102.58, 54.9) * mm, "end": v(117.58, 54.9) * mm});
            skLineSegment(sketch, "E56.left", {"start": v(102.58, 69.9) * mm, "end": v(102.58, 54.9) * mm});
            skLineSegment(sketch, "E56.right", {"start": v(117.58, 69.9) * mm, "end": v(117.58, 54.9) * mm});
            skLineSegment(sketch, "E57.bottom", {"start": v(138.58, 69.9) * mm, "end": v(153.58, 69.9) * mm});
            skLineSegment(sketch, "E57.top", {"start": v(138.58, 54.9) * mm, "end": v(153.58, 54.9) * mm});
            skLineSegment(sketch, "E57.left", {"start": v(138.58, 69.9) * mm, "end": v(138.58, 54.9) * mm});
            skLineSegment(sketch, "E57.right", {"start": v(153.58, 69.9) * mm, "end": v(153.58, 54.9) * mm});
            skSolve(sketch);
        }
        {
            var Q0;
            Q0=qSketchRegion(id+"F48",true);
            extrude(context, id + "F49", {"entities" : qUnion([Q0]), "operationType" : NewBodyOperationType.ADD, "depth" : 1 * mm, "offsetDistance" : 25 * mm});
        }
        {
            var Q0;
            Q0=makeQuery(id+"F40.opExtrude","SWEPT_BODY",BODY,{"disambiguationData":[OSD([sQuery(id+"F39.wireOp",EDGE,"E44.bottom"),sQuery(id+"F39.wireOp",EDGE,"E44.top"),sQuery(id+"F39.wireOp",EDGE,"E44.left"),sQuery(id+"F39.wireOp",EDGE,"E44.right"),sQuery(id+"F39.wireOp",EDGE,"E45"),sQuery(id+"F39.wireOp",EDGE,"E46")])]});
            deleteBodies(context, id + "F50", {"entities" : qUnion([Q0])});
        }
        {
            var Q0;
            Q0=qCreatedBy(id+"F19.planeOp",FACE);
            var sketch = newSketch(context, id + "F51", { "sketchPlane" : qUnion([Q0])});
            skLineSegment(sketch, "E58.bottom", {"start": v(95.11, 78.4) * mm, "end": v(168.61, 78.4) * mm});
            skLineSegment(sketch, "E58.top", {"start": v(95.11, 46.4) * mm, "end": v(168.61, 46.4) * mm});
            skLineSegment(sketch, "E58.left", {"start": v(95.11, 78.4) * mm, "end": v(95.11, 46.4) * mm});
            skLineSegment(sketch, "E58.right", {"start": v(168.61, 78.4) * mm, "end": v(168.61, 46.4) * mm});
            skSolve(sketch);
        }
        {
            var Q0;
            Q0=makeQuery(id+"F18.opExtrude","CAP_FACE",FACE,{"disambiguationData":[OSD([sQuery(id+"F17.wireOp",EDGE,"E25.bottom"),sQuery(id+"F17.wireOp",EDGE,"E25.top"),sQuery(id+"F17.wireOp",EDGE,"E25.left"),sQuery(id+"F17.wireOp",EDGE,"E25.right"),sQuery(id+"F17.wireOp",EDGE,"E26.filletArc")])],"isStart":false});
            var sketch = newSketch(context, id + "F52", { "sketchPlane" : qUnion([Q0])});
            skLineSegment(sketch, "E59.bottom", {"start": v(-169.42, 78.5) * mm, "end": v(-95.92, 78.5) * mm});
            skLineSegment(sketch, "E59.top", {"start": v(-169.42, 46.5) * mm, "end": v(-95.92, 46.5) * mm});
            skLineSegment(sketch, "E59.left", {"start": v(-169.42, 78.5) * mm, "end": v(-169.42, 46.5) * mm});
            skLineSegment(sketch, "E59.right", {"start": v(-95.92, 78.5) * mm, "end": v(-95.92, 46.5) * mm});
            skSolve(sketch);
        }
        {
            var Q0;
            Q0=qSketchRegion(id+"F51",true);
            extrude(context, id + "F53", {"entities" : qUnion([Q0]), "operationType" : NewBodyOperationType.ADD, "depth" : 19.6 * mm, "offsetDistance" : 25 * mm});
        }
        {
            var Q0;
            Q0=qSketchRegion(id+"F52",true);
            extrude(context, id + "F54", {"entities" : qUnion([Q0]), "operationType" : NewBodyOperationType.ADD, "depth" : 19.6 * mm, "offsetDistance" : 25 * mm});
        }
        {
            var Q0;
            Q0=makeQuery(id+"F53.boolean.opBoolean","MERGE",FACE,{"derivedFrom":[makeQuery(id+"F21.opExtrude","CAP_FACE",FACE,{"disambiguationData":[OSD([sQuery(id+"F20.wireOp",EDGE,"E27.bottom"),sQuery(id+"F20.wireOp",EDGE,"E27.top"),sQuery(id+"F20.wireOp",EDGE,"E27.left"),sQuery(id+"F20.wireOp",EDGE,"E27.right"),sQuery(id+"F20.wireOp",EDGE,"E28.filletArc")])],"isStart":false}),makeQuery(id+"F53.opExtrude","CAP_FACE",FACE,{"disambiguationData":[OSD([sQuery(id+"F51.wireOp",EDGE,"E58.bottom"),sQuery(id+"F51.wireOp",EDGE,"E58.top"),sQuery(id+"F51.wireOp",EDGE,"E58.left"),sQuery(id+"F51.wireOp",EDGE,"E58.right")])],"isStart":false})]});
            var sketch = newSketch(context, id + "F55", { "sketchPlane" : qUnion([Q0])});
            skLineSegment(sketch, "E60.bottom", {"start": v(101.08, 71.4) * mm, "end": v(119.08, 71.4) * mm});
            skLineSegment(sketch, "E60.top", {"start": v(101.08, 53.4) * mm, "end": v(119.08, 53.4) * mm});
            skLineSegment(sketch, "E60.left", {"start": v(101.08, 71.4) * mm, "end": v(101.08, 53.4) * mm});
            skLineSegment(sketch, "E60.right", {"start": v(119.08, 71.4) * mm, "end": v(119.08, 53.4) * mm});
            skLineSegment(sketch, "E61.bottom", {"start": v(137.08, 71.4) * mm, "end": v(155.08, 71.4) * mm});
            skLineSegment(sketch, "E61.top", {"start": v(137.08, 53.4) * mm, "end": v(155.08, 53.4) * mm});
            skLineSegment(sketch, "E61.left", {"start": v(137.08, 71.4) * mm, "end": v(137.08, 53.4) * mm});
            skLineSegment(sketch, "E61.right", {"start": v(155.08, 71.4) * mm, "end": v(155.08, 53.4) * mm});
            skSolve(sketch);
        }
        {
            var Q0;
            Q0=makeQuery(id+"F54.boolean.opBoolean","MERGE",FACE,{"derivedFrom":[makeQuery(id+"F24.opExtrude","CAP_FACE",FACE,{"disambiguationData":[OSD([sQuery(id+"F23.wireOp",EDGE,"E29.bottom"),sQuery(id+"F23.wireOp",EDGE,"E29.top"),sQuery(id+"F23.wireOp",EDGE,"E29.left"),sQuery(id+"F23.wireOp",EDGE,"E29.right"),sQuery(id+"F23.wireOp",EDGE,"E30.filletArc")])],"isStart":false}),makeQuery(id+"F54.opExtrude","CAP_FACE",FACE,{"disambiguationData":[OSD([sQuery(id+"F52.wireOp",EDGE,"E59.bottom"),sQuery(id+"F52.wireOp",EDGE,"E59.top"),sQuery(id+"F52.wireOp",EDGE,"E59.left"),sQuery(id+"F52.wireOp",EDGE,"E59.right")])],"isStart":false})]});
            var sketch = newSketch(context, id + "F56", { "sketchPlane" : qUnion([Q0])});
            skLineSegment(sketch, "E62.bottom", {"start": v(-155.9, 71.5) * mm, "end": v(-137.9, 71.5) * mm});
            skLineSegment(sketch, "E62.top", {"start": v(-155.9, 53.5) * mm, "end": v(-137.9, 53.5) * mm});
            skLineSegment(sketch, "E62.left", {"start": v(-155.9, 71.5) * mm, "end": v(-155.9, 53.5) * mm});
            skLineSegment(sketch, "E62.right", {"start": v(-137.9, 71.5) * mm, "end": v(-137.9, 53.5) * mm});
            skLineSegment(sketch, "E63.top", {"start": v(-119.9, 53.5) * mm, "end": v(-101.9, 53.5) * mm});
            skLineSegment(sketch, "E63.left", {"start": v(-119.9, 71.5) * mm, "end": v(-119.9, 53.5) * mm});
            skLineSegment(sketch, "E63.right", {"start": v(-101.9, 71.5) * mm, "end": v(-101.9, 53.5) * mm});
            skLineSegment(sketch, "E64", {"start": v(-119.9, 71.5) * mm, "end": v(-101.9, 71.5) * mm});
            skSolve(sketch);
        }
        {
            var Q0;
            Q0=makeQuery(id+"F55.imprint","IMPRINT",FACE,{"disambiguationData":[TD([[makeQuery(id+"F55.imprint","IMPRINT",EDGE,{"derivedFrom":sQuery(id+"F55.wireOp",EDGE,"E60.bottom")}),-1.0]])]});
            var sketch = newSketch(context, id + "F57", { "sketchPlane" : qUnion([Q0])});
            skLineSegment(sketch, "E65.bottom", {"start": v(99.08, 73.4) * mm, "end": v(121.08, 73.4) * mm});
            skLineSegment(sketch, "E65.top", {"start": v(99.08, 51.4) * mm, "end": v(121.08, 51.4) * mm});
            skLineSegment(sketch, "E65.left", {"start": v(99.08, 73.4) * mm, "end": v(99.08, 51.4) * mm});
            skLineSegment(sketch, "E65.right", {"start": v(121.08, 73.4) * mm, "end": v(121.08, 51.4) * mm});
            skLineSegment(sketch, "E66.bottom", {"start": v(135.08, 73.4) * mm, "end": v(157.08, 73.4) * mm});
            skLineSegment(sketch, "E66.top", {"start": v(135.08, 51.4) * mm, "end": v(157.08, 51.4) * mm});
            skLineSegment(sketch, "E66.left", {"start": v(135.08, 73.4) * mm, "end": v(135.08, 51.4) * mm});
            skLineSegment(sketch, "E66.right", {"start": v(157.08, 73.4) * mm, "end": v(157.08, 51.4) * mm});
            skSolve(sketch);
        }
        {
            var Q0;
            Q0=makeQuery(id+"F56.imprint","IMPRINT",FACE,{"disambiguationData":[TD([[makeQuery(id+"F56.imprint","IMPRINT",EDGE,{"derivedFrom":sQuery(id+"F56.wireOp",EDGE,"E62.bottom")}),1.0]])]});
            var sketch = newSketch(context, id + "F58", { "sketchPlane" : qUnion([Q0])});
            skLineSegment(sketch, "E67.bottom", {"start": v(-157.9, 73.5) * mm, "end": v(-135.9, 73.5) * mm});
            skLineSegment(sketch, "E67.top", {"start": v(-157.9, 51.5) * mm, "end": v(-135.9, 51.5) * mm});
            skLineSegment(sketch, "E67.left", {"start": v(-157.9, 73.5) * mm, "end": v(-157.9, 51.5) * mm});
            skLineSegment(sketch, "E67.right", {"start": v(-135.9, 73.5) * mm, "end": v(-135.9, 51.5) * mm});
            skLineSegment(sketch, "E68.bottom", {"start": v(-121.9, 73.5) * mm, "end": v(-99.9, 73.5) * mm});
            skLineSegment(sketch, "E68.top", {"start": v(-121.9, 51.5) * mm, "end": v(-99.9, 51.5) * mm});
            skLineSegment(sketch, "E68.left", {"start": v(-121.9, 73.5) * mm, "end": v(-121.9, 51.5) * mm});
            skLineSegment(sketch, "E68.right", {"start": v(-99.9, 73.5) * mm, "end": v(-99.9, 51.5) * mm});
            skSolve(sketch);
        }
        {
            var Q0;
            Q0=qSketchRegion(id+"F57",true);
            extrude(context, id + "F59", {"entities" : qUnion([Q0]), "operationType" : NewBodyOperationType.REMOVE, "oppositeDirection" : true, "depth" : 3 * mm, "offsetDistance" : 25 * mm});
        }
        {
            var Q0;
            Q0=qSketchRegion(id+"F58",true);
            extrude(context, id + "F60", {"entities" : qUnion([Q0]), "operationType" : NewBodyOperationType.REMOVE, "oppositeDirection" : true, "depth" : 3 * mm, "offsetDistance" : 25 * mm});
        }
        {
            var Q0;
            Q0=qCreatedBy(id+"F41.planeOp",FACE);
            var sketch = newSketch(context, id + "F61", { "sketchPlane" : qUnion([Q0])});
            skLineSegment(sketch, "E69.bottom", {"start": v(139.08, 69.4) * mm, "end": v(153.08, 69.4) * mm});
            skLineSegment(sketch, "E69.top", {"start": v(139.08, 63.4) * mm, "end": v(153.08, 63.4) * mm});
            skLineSegment(sketch, "E69.left", {"start": v(139.08, 69.4) * mm, "end": v(139.08, 63.4) * mm});
            skLineSegment(sketch, "E69.right", {"start": v(153.08, 69.4) * mm, "end": v(153.08, 63.4) * mm});
            skLineSegment(sketch, "E70.bottom", {"start": v(139.08, 61.4) * mm, "end": v(153.08, 61.4) * mm});
            skLineSegment(sketch, "E70.top", {"start": v(139.08, 55.4) * mm, "end": v(153.08, 55.4) * mm});
            skLineSegment(sketch, "E70.left", {"start": v(139.08, 61.4) * mm, "end": v(139.08, 55.4) * mm});
            skLineSegment(sketch, "E70.right", {"start": v(153.08, 61.4) * mm, "end": v(153.08, 55.4) * mm});
            skLineSegment(sketch, "E71.bottom", {"start": v(137.33, 71.15) * mm, "end": v(154.83, 71.15) * mm});
            skLineSegment(sketch, "E71.top", {"start": v(137.33, 53.65) * mm, "end": v(154.83, 53.65) * mm});
            skLineSegment(sketch, "E71.left", {"start": v(137.33, 71.15) * mm, "end": v(137.33, 53.65) * mm});
            skLineSegment(sketch, "E71.right", {"start": v(154.83, 71.15) * mm, "end": v(154.83, 53.65) * mm});
            skSolve(sketch);
        }
        {
            var Q0;
            Q0=qSketchRegion(id+"F55",true);
            extrude(context, id + "F62", {"entities" : qUnion([Q0]), "operationType" : NewBodyOperationType.REMOVE, "oppositeDirection" : true, "depth" : 22.6 * mm, "offsetDistance" : 25 * mm});
        }
        {
            var Q0;
            Q0=qSketchRegion(id+"F56",true);
            extrude(context, id + "F63", {"entities" : qUnion([Q0]), "operationType" : NewBodyOperationType.REMOVE, "oppositeDirection" : true, "depth" : 22.6 * mm, "offsetDistance" : 25 * mm});
        }
        {
            var Q0;
            Q0=makeQuery(id+"F63.boolean.opBoolean","COPY",FACE,{"derivedFrom":makeQuery(id+"F63.opExtrude","CAP_FACE",FACE,{"disambiguationData":[OSD([sQuery(id+"F56.wireOp",EDGE,"E63.top"),sQuery(id+"F56.wireOp",EDGE,"E63.left"),sQuery(id+"F56.wireOp",EDGE,"E63.right"),sQuery(id+"F56.wireOp",EDGE,"E64")])],"isStart":false})});
            var sketch = newSketch(context, id + "F64", { "sketchPlane" : qUnion([Q0])});
            skCircle(sketch, "E72", {"center": v(110.08, 62.4) * mm, "radius": 7 * mm});
            skCircle(sketch, "E73", {"center": v(146.08, 62.4) * mm, "radius": 7 * mm});
            skSolve(sketch);
        }
        {
            var Q0;
            Q0=makeQuery(id+"F64.imprint","IMPRINT",FACE,{"disambiguationData":[TD([[makeQuery(id+"F64.imprint","IMPRINT",EDGE,{"derivedFrom":makeQuery(id+"F63.boolean.opBoolean","COPY",EDGE,{"derivedFrom":makeQuery(id+"F63.opExtrude","CAP_EDGE",EDGE,{"disambiguationData":[OSD([sQuery(id+"F56.wireOp",EDGE,"E63.top")])],"isStart":false})})}),1.0]])]});
            var sketch = newSketch(context, id + "F65", { "sketchPlane" : qUnion([Q0])});
            skCircle(sketch, "E74", {"center": v(-110.9, 62.5) * mm, "radius": 7 * mm});
            skCircle(sketch, "E75", {"center": v(-146.9, 62.5) * mm, "radius": 7 * mm});
            skSolve(sketch);
        }
        {
            var Q0;
            Q0=qSketchRegion(id+"F64",true);
            extrude(context, id + "F66", {"entities" : qUnion([Q0]), "operationType" : NewBodyOperationType.REMOVE, "oppositeDirection" : true, "depth" : 5 * mm, "offsetDistance" : 25 * mm});
        }
        {
            var Q0;
            Q0=qSketchRegion(id+"F65",true);
            extrude(context, id + "F67", {"entities" : qUnion([Q0]), "operationType" : NewBodyOperationType.REMOVE, "oppositeDirection" : true, "depth" : 5 * mm, "offsetDistance" : 25 * mm});
        }
        {
            var Q0;
            Q0=qSketchRegion(id+"F61",true);
            extrude(context, id + "F68", {"entities" : qUnion([Q0]), "oppositeDirection" : true, "depth" : 17.6 * mm, "offsetDistance" : 25 * mm});
        }
        {
            var Q0;
            Q0=qCreatedBy(id+"F41.planeOp",FACE);
            var sketch = newSketch(context, id + "F69", { "sketchPlane" : qUnion([Q0])});
            skLineSegment(sketch, "E76.bottom", {"start": v(135.33, 73.15) * mm, "end": v(156.83, 73.15) * mm});
            skLineSegment(sketch, "E76.top", {"start": v(135.33, 51.65) * mm, "end": v(156.83, 51.65) * mm});
            skLineSegment(sketch, "E76.left", {"start": v(135.33, 73.15) * mm, "end": v(135.33, 51.65) * mm});
            skLineSegment(sketch, "E76.right", {"start": v(156.83, 73.15) * mm, "end": v(156.83, 51.65) * mm});
            skLineSegment(sketch, "E77.bottom", {"start": v(139.08, 69.4) * mm, "end": v(153.08, 69.4) * mm});
            skLineSegment(sketch, "E77.top", {"start": v(139.08, 63.4) * mm, "end": v(153.08, 63.4) * mm});
            skLineSegment(sketch, "E77.left", {"start": v(139.08, 69.4) * mm, "end": v(139.08, 63.4) * mm});
            skLineSegment(sketch, "E77.right", {"start": v(153.08, 69.4) * mm, "end": v(153.08, 63.4) * mm});
            skLineSegment(sketch, "E78.bottom", {"start": v(139.08, 61.4) * mm, "end": v(153.08, 61.4) * mm});
            skLineSegment(sketch, "E78.top", {"start": v(139.08, 55.4) * mm, "end": v(153.08, 55.4) * mm});
            skLineSegment(sketch, "E78.left", {"start": v(139.08, 61.4) * mm, "end": v(139.08, 55.4) * mm});
            skLineSegment(sketch, "E78.right", {"start": v(153.08, 61.4) * mm, "end": v(153.08, 55.4) * mm});
            skSolve(sketch);
        }
        {
            var Q0;
            Q0=qSketchRegion(id+"F69",true);
            extrude(context, id + "F70", {"entities" : qUnion([Q0]), "operationType" : NewBodyOperationType.ADD, "depth" : 3 * mm, "offsetDistance" : 25 * mm});
        }
        {
            var Q0;
            Q0=makeQuery(id+"F68.opExtrude","CAP_FACE",FACE,{"disambiguationData":[OSD([sQuery(id+"F61.wireOp",EDGE,"E69.bottom"),sQuery(id+"F61.wireOp",EDGE,"E69.top"),sQuery(id+"F61.wireOp",EDGE,"E69.left"),sQuery(id+"F61.wireOp",EDGE,"E69.right"),sQuery(id+"F61.wireOp",EDGE,"E70.bottom"),sQuery(id+"F61.wireOp",EDGE,"E70.top"),sQuery(id+"F61.wireOp",EDGE,"E70.left"),sQuery(id+"F61.wireOp",EDGE,"E70.right"),sQuery(id+"F61.wireOp",EDGE,"E71.bottom"),sQuery(id+"F61.wireOp",EDGE,"E71.top"),sQuery(id+"F61.wireOp",EDGE,"E71.left"),sQuery(id+"F61.wireOp",EDGE,"E71.right")])],"isStart":false});
            cPlane(context, id + "F71", {"entities" : qUnion([Q0]), "cplaneType" : CPlaneType.OFFSET, "offset" : 10 * mm, "width" : 150 * mm, "height" : 150 * mm});
        }
        {
            var Q0;
            Q0=qCreatedBy(id+"F71.planeOp",FACE);
            var sketch = newSketch(context, id + "F72", { "sketchPlane" : qUnion([Q0])});
            skLineSegment(sketch, "E79.bottom", {"start": v(137.33, -71.15) * mm, "end": v(154.83, -71.15) * mm});
            skLineSegment(sketch, "E79.top", {"start": v(137.33, -53.65) * mm, "end": v(154.83, -53.65) * mm});
            skLineSegment(sketch, "E79.left", {"start": v(137.33, -71.15) * mm, "end": v(137.33, -53.65) * mm});
            skLineSegment(sketch, "E79.right", {"start": v(154.83, -71.15) * mm, "end": v(154.83, -53.65) * mm});
            skLineSegment(sketch, "E80.bottom", {"start": v(139.08, -69.4) * mm, "end": v(145.08, -69.4) * mm});
            skLineSegment(sketch, "E80.top", {"start": v(139.08, -67.4) * mm, "end": v(145.08, -67.4) * mm});
            skLineSegment(sketch, "E80.left", {"start": v(139.08, -69.4) * mm, "end": v(139.08, -67.4) * mm});
            skLineSegment(sketch, "E80.right", {"start": v(145.08, -69.4) * mm, "end": v(145.08, -67.4) * mm});
            skLineSegment(sketch, "E81.bottom", {"start": v(147.08, -69.4) * mm, "end": v(153.08, -69.4) * mm});
            skLineSegment(sketch, "E81.top", {"start": v(147.08, -67.4) * mm, "end": v(153.08, -67.4) * mm});
            skLineSegment(sketch, "E81.left", {"start": v(147.08, -69.4) * mm, "end": v(147.08, -67.4) * mm});
            skLineSegment(sketch, "E81.right", {"start": v(153.08, -69.4) * mm, "end": v(153.08, -67.4) * mm});
            skLineSegment(sketch, "E82.bottom", {"start": v(139.08, -65.4) * mm, "end": v(145.08, -65.4) * mm});
            skLineSegment(sketch, "E82.top", {"start": v(139.08, -63.4) * mm, "end": v(145.08, -63.4) * mm});
            skLineSegment(sketch, "E82.left", {"start": v(139.08, -65.4) * mm, "end": v(139.08, -63.4) * mm});
            skLineSegment(sketch, "E82.right", {"start": v(145.08, -65.4) * mm, "end": v(145.08, -63.4) * mm});
            skLineSegment(sketch, "E83.bottom", {"start": v(147.08, -65.4) * mm, "end": v(153.08, -65.4) * mm});
            skLineSegment(sketch, "E83.top", {"start": v(147.08, -63.4) * mm, "end": v(153.08, -63.4) * mm});
            skLineSegment(sketch, "E83.left", {"start": v(147.08, -65.4) * mm, "end": v(147.08, -63.4) * mm});
            skLineSegment(sketch, "E83.right", {"start": v(153.08, -65.4) * mm, "end": v(153.08, -63.4) * mm});
            skLineSegment(sketch, "E84.bottom", {"start": v(139.08, -61.4) * mm, "end": v(145.08, -61.4) * mm});
            skLineSegment(sketch, "E84.top", {"start": v(139.08, -59.4) * mm, "end": v(145.08, -59.4) * mm});
            skLineSegment(sketch, "E84.left", {"start": v(139.08, -61.4) * mm, "end": v(139.08, -59.4) * mm});
            skLineSegment(sketch, "E84.right", {"start": v(145.08, -61.4) * mm, "end": v(145.08, -59.4) * mm});
            skLineSegment(sketch, "E85.bottom", {"start": v(147.08, -61.4) * mm, "end": v(153.08, -61.4) * mm});
            skLineSegment(sketch, "E85.top", {"start": v(147.08, -59.4) * mm, "end": v(153.08, -59.4) * mm});
            skLineSegment(sketch, "E85.left", {"start": v(147.08, -61.4) * mm, "end": v(147.08, -59.4) * mm});
            skLineSegment(sketch, "E85.right", {"start": v(153.08, -61.4) * mm, "end": v(153.08, -59.4) * mm});
            skLineSegment(sketch, "E86.bottom", {"start": v(139.08, -57.4) * mm, "end": v(145.08, -57.4) * mm});
            skLineSegment(sketch, "E86.top", {"start": v(139.08, -55.4) * mm, "end": v(145.08, -55.4) * mm});
            skLineSegment(sketch, "E86.left", {"start": v(139.08, -57.4) * mm, "end": v(139.08, -55.4) * mm});
            skLineSegment(sketch, "E86.right", {"start": v(145.08, -57.4) * mm, "end": v(145.08, -55.4) * mm});
            skLineSegment(sketch, "E87.bottom", {"start": v(147.08, -57.4) * mm, "end": v(153.08, -57.4) * mm});
            skLineSegment(sketch, "E87.top", {"start": v(147.08, -55.4) * mm, "end": v(153.08, -55.4) * mm});
            skLineSegment(sketch, "E87.left", {"start": v(147.08, -57.4) * mm, "end": v(147.08, -55.4) * mm});
            skLineSegment(sketch, "E87.right", {"start": v(153.08, -57.4) * mm, "end": v(153.08, -55.4) * mm});
            skSolve(sketch);
        }
        {
            var Q0;
            Q0=qSketchRegion(id+"F72",true);
            extrude(context, id + "F73", {"entities" : qUnion([Q0]), "oppositeDirection" : true, "depth" : 2 * mm, "offsetDistance" : 25 * mm});
        }
        {
            var Q0;
            Q0=makeQuery(id+"F73.opExtrude","CAP_FACE",FACE,{"disambiguationData":[OSD([sQuery(id+"F72.wireOp",EDGE,"E79.bottom"),sQuery(id+"F72.wireOp",EDGE,"E79.top"),sQuery(id+"F72.wireOp",EDGE,"E79.left"),sQuery(id+"F72.wireOp",EDGE,"E79.right"),sQuery(id+"F72.wireOp",EDGE,"E80.bottom"),sQuery(id+"F72.wireOp",EDGE,"E80.top"),sQuery(id+"F72.wireOp",EDGE,"E80.left"),sQuery(id+"F72.wireOp",EDGE,"E80.right"),sQuery(id+"F72.wireOp",EDGE,"E81.bottom"),sQuery(id+"F72.wireOp",EDGE,"E81.top"),sQuery(id+"F72.wireOp",EDGE,"E81.left"),sQuery(id+"F72.wireOp",EDGE,"E81.right"),sQuery(id+"F72.wireOp",EDGE,"E82.bottom"),sQuery(id+"F72.wireOp",EDGE,"E82.top"),sQuery(id+"F72.wireOp",EDGE,"E82.left"),sQuery(id+"F72.wireOp",EDGE,"E82.right"),sQuery(id+"F72.wireOp",EDGE,"E83.bottom"),sQuery(id+"F72.wireOp",EDGE,"E83.top"),sQuery(id+"F72.wireOp",EDGE,"E83.left"),sQuery(id+"F72.wireOp",EDGE,"E83.right"),sQuery(id+"F72.wireOp",EDGE,"E84.bottom"),sQuery(id+"F72.wireOp",EDGE,"E84.top"),sQuery(id+"F72.wireOp",EDGE,"E84.left"),sQuery(id+"F72.wireOp",EDGE,"E84.right"),sQuery(id+"F72.wireOp",EDGE,"E85.bottom"),sQuery(id+"F72.wireOp",EDGE,"E85.top"),sQuery(id+"F72.wireOp",EDGE,"E85.left"),sQuery(id+"F72.wireOp",EDGE,"E85.right"),sQuery(id+"F72.wireOp",EDGE,"E86.bottom"),sQuery(id+"F72.wireOp",EDGE,"E86.top"),sQuery(id+"F72.wireOp",EDGE,"E86.left"),sQuery(id+"F72.wireOp",EDGE,"E86.right"),sQuery(id+"F72.wireOp",EDGE,"E87.bottom"),sQuery(id+"F72.wireOp",EDGE,"E87.top"),sQuery(id+"F72.wireOp",EDGE,"E87.left"),sQuery(id+"F72.wireOp",EDGE,"E87.right")])],"isStart":false});
            var sketch = newSketch(context, id + "F74", { "sketchPlane" : qUnion([Q0])});
            skLineSegment(sketch, "E88.bottom", {"start": v(145.08, 67.4) * mm, "end": v(147.08, 67.4) * mm});
            skLineSegment(sketch, "E88.top", {"start": v(145.08, 65.4) * mm, "end": v(147.08, 65.4) * mm});
            skLineSegment(sketch, "E88.left", {"start": v(145.08, 67.4) * mm, "end": v(145.08, 65.4) * mm});
            skLineSegment(sketch, "E88.right", {"start": v(147.08, 67.4) * mm, "end": v(147.08, 65.4) * mm});
            skLineSegment(sketch, "E89.bottom", {"start": v(145.08, 59.4) * mm, "end": v(147.08, 59.4) * mm});
            skLineSegment(sketch, "E89.top", {"start": v(145.08, 57.4) * mm, "end": v(147.08, 57.4) * mm});
            skLineSegment(sketch, "E89.left", {"start": v(145.08, 59.4) * mm, "end": v(145.08, 57.4) * mm});
            skLineSegment(sketch, "E89.right", {"start": v(147.08, 59.4) * mm, "end": v(147.08, 57.4) * mm});
            skSolve(sketch);
        }
        {
            var Q0;
            Q0=qSketchRegion(id+"F74",true);
            extrude(context, id + "F75", {"entities" : qUnion([Q0]), "operationType" : NewBodyOperationType.ADD, "depth" : 2 * mm, "offsetDistance" : 25 * mm});
        }
        {
            var Q0;
            Q0=makeQuery(id+"F53.boolean.opBoolean","MERGE",FACE,{"derivedFrom":[makeQuery(id+"F21.opExtrude","CAP_FACE",FACE,{"disambiguationData":[OSD([sQuery(id+"F20.wireOp",EDGE,"E27.bottom"),sQuery(id+"F20.wireOp",EDGE,"E27.top"),sQuery(id+"F20.wireOp",EDGE,"E27.left"),sQuery(id+"F20.wireOp",EDGE,"E27.right"),sQuery(id+"F20.wireOp",EDGE,"E28.filletArc")])],"isStart":false}),makeQuery(id+"F53.opExtrude","CAP_FACE",FACE,{"disambiguationData":[OSD([sQuery(id+"F51.wireOp",EDGE,"E58.bottom"),sQuery(id+"F51.wireOp",EDGE,"E58.top"),sQuery(id+"F51.wireOp",EDGE,"E58.left"),sQuery(id+"F51.wireOp",EDGE,"E58.right")])],"isStart":false})]});
            var sketch = newSketch(context, id + "F76", { "sketchPlane" : qUnion([Q0])});
            skPoint(sketch, "E90", {"position": v(128.1, 62.88) * mm});
            skPoint(sketch, "E91", {"position": v(164.13, 62.88) * mm});
            skPoint(sketch, "E92", {"position": v(-128.9, 62.89) * mm});
            skPoint(sketch, "E93", {"position": v(-164.92, 62.89) * mm});
            skSolve(sketch);
        }
        {
            var Q0;
            Q0=sQuery(id+"F76.wireOp",VERTEX,"E91");
            var Q1;
            Q1=sQuery(id+"F76.wireOp",VERTEX,"E90");
            var Q2;
            Q2=sQuery(id+"F76.wireOp",VERTEX,"E92");
            var Q3;
            Q3=sQuery(id+"F76.wireOp",VERTEX,"E93");
            var Q4;
            Q4=makeQuery(id+"F12.opExtrude","SWEPT_BODY",BODY,{"disambiguationData":[OSD([sQuery(id+"F11.wireOp",EDGE,"E18.bottom"),sQuery(id+"F11.wireOp",EDGE,"E18.top"),sQuery(id+"F11.wireOp",EDGE,"E18.left"),sQuery(id+"F11.wireOp",EDGE,"E18.right"),sQuery(id+"F11.wireOp",EDGE,"E20.filletArc")])]});
            var Q5;
            Q5=makeQuery(id+"F12.opExtrude","SWEPT_BODY",BODY,{"disambiguationData":[OSD([sQuery(id+"F11.wireOp",EDGE,"E19.bottom"),sQuery(id+"F11.wireOp",EDGE,"E19.top"),sQuery(id+"F11.wireOp",EDGE,"E19.left"),sQuery(id+"F11.wireOp",EDGE,"E19.right"),sQuery(id+"F11.wireOp",EDGE,"E21.filletArc")])]});
            hole(context, id + "F77", {"style" : HoleStyle.SIMPLE, "endStyle" : HoleEndStyle.BLIND, "holeDiameter" : 2.4 * mm, "holeDepth" : 13 * mm, "tappedDepth" : 12 * mm, "tapClearance" : 3, "locations" : qUnion([Q0, Q1, Q2, Q3]), "scope" : qUnion([Q4, Q5])});
        }
        {
            var Q0;
            Q0=makeQuery(id+"F12.opExtrude","CAP_FACE",FACE,{"disambiguationData":[OSD([sQuery(id+"F11.wireOp",EDGE,"E18.bottom"),sQuery(id+"F11.wireOp",EDGE,"E18.top"),sQuery(id+"F11.wireOp",EDGE,"E18.left"),sQuery(id+"F11.wireOp",EDGE,"E18.right"),sQuery(id+"F11.wireOp",EDGE,"E20.filletArc")])],"isStart":true});
            cPlane(context, id + "F78", {"entities" : qUnion([Q0]), "cplaneType" : CPlaneType.OFFSET, "offset" : 25 * mm, "width" : 150 * mm, "height" : 150 * mm});
        }
        {
            var Q0;
            Q0=qCreatedBy(id+"F78.planeOp",FACE);
            var sketch = newSketch(context, id + "F79", { "sketchPlane" : qUnion([Q0])});
            skLineSegment(sketch, "E94.bottom", {"start": v(53.11, -35.98) * mm, "end": v(172.11, -35.98) * mm});
            skLineSegment(sketch, "E94.top", {"start": v(66.11, -81.9) * mm, "end": v(172.11, -81.9) * mm});
            skLineSegment(sketch, "E94.left", {"start": v(53.11, -35.98) * mm, "end": v(53.11, -68.9) * mm});
            skLineSegment(sketch, "E94.right", {"start": v(172.11, -35.98) * mm, "end": v(172.11, -81.9) * mm});
            skPoint(sketch, "E95.visualSharp", {"position": v(53.11, -81.9) * mm});
            skArc(sketch, "E95.filletArc", {"start": v(53.11, -68.9) * mm, "mid": v(56.92, -78.09) * mm, "end": v(66.11, -81.9) * mm});
            skSolve(sketch);
        }
        {
            var Q0;
            Q0=qSketchRegion(id+"F79",true);
            extrude(context, id + "F80", {"entities" : qUnion([Q0]), "depth" : 2 * mm, "offsetDistance" : 25 * mm});
        }
        {
            var Q0;
            Q0=makeQuery(id+"F80.opExtrude","SWEPT_FACE",FACE,{"disambiguationData":[OSD([sQuery(id+"F79.wireOp",EDGE,"E94.right")])]});
            var sketch = newSketch(context, id + "F81", { "sketchPlane" : qUnion([Q0])});
            skLineSegment(sketch, "E96", {"start": v(57.23, -94.85) * mm, "end": v(35.98, -71.6) * mm});
            skLineSegment(sketch, "E97", {"start": v(35.98, -71.6) * mm, "end": v(81.9, -71.6) * mm});
            skLineSegment(sketch, "E98", {"start": v(81.9, -71.6) * mm, "end": v(81.9, -72.6) * mm});
            skLineSegment(sketch, "E99", {"start": v(81.9, -72.6) * mm, "end": v(40.96, -72.6) * mm});
            skLineSegment(sketch, "E100", {"start": v(40.96, -72.6) * mm, "end": v(59.44, -92.83) * mm});
            skLineSegment(sketch, "E101", {"start": v(59.44, -92.83) * mm, "end": v(57.23, -94.85) * mm});
            skSolve(sketch);
        }
        {
            var Q0;
            Q0=qSketchRegion(id+"F81",true);
            extrude(context, id + "F82", {"entities" : qUnion([Q0]), "operationType" : NewBodyOperationType.ADD, "oppositeDirection" : true, "depth" : 119 * mm, "offsetDistance" : 25 * mm});
        }
        {
            var Q0;
            Q0=makeQuery(id+"F82.opExtrude","CAP_EDGE",EDGE,{"disambiguationData":[OSD([sQuery(id+"F81.wireOp",EDGE,"E98")])],"isStart":false});
            fillet(context, id + "F83", {"entities" : qUnion([Q0]), "radius" : 13 * mm, "tangentPropagation" : true, "allowEdgeOverflow" : false});
        }
        {
            var Q0;
            Q0=makeQuery(id+"F80.opExtrude","CAP_FACE",FACE,{"disambiguationData":[OSD([sQuery(id+"F79.wireOp",EDGE,"E94.bottom"),sQuery(id+"F79.wireOp",EDGE,"E94.top"),sQuery(id+"F79.wireOp",EDGE,"E94.left"),sQuery(id+"F79.wireOp",EDGE,"E94.right"),sQuery(id+"F79.wireOp",EDGE,"E95.filletArc")])],"isStart":true});
            var sketch = newSketch(context, id + "F84", { "sketchPlane" : qUnion([Q0])});
            skCircle(sketch, "E102", {"center": v(78.08, 59.4) * mm, "radius": 2.5 * mm});
            skCircle(sketch, "E103", {"center": v(110.1, 58.98) * mm, "radius": 2.5 * mm});
            skCircle(sketch, "E104", {"center": v(142.58, 59.4) * mm, "radius": 2.5 * mm});
            skSolve(sketch);
        }
        {
            var Q0;
            Q0=qSketchRegion(id+"F84",true);
            extrude(context, id + "F85", {"entities" : qUnion([Q0]), "operationType" : NewBodyOperationType.REMOVE, "oppositeDirection" : true, "depth" : 3 * mm, "offsetDistance" : 25 * mm});
        }
        {
            var Q0;
            Q0=makeQuery(id+"F82.opExtrude","SWEPT_FACE",FACE,{"disambiguationData":[OSD([sQuery(id+"F81.wireOp",EDGE,"E96")])]});
            var sketch = newSketch(context, id + "F86", { "sketchPlane" : qUnion([Q0])});
            skPoint(sketch, "E105", {"position": v(71.66, -98.62) * mm});
            skPoint(sketch, "E106", {"position": v(71.66, -83.62) * mm});
            skPoint(sketch, "E107", {"position": v(152.91, -98.62) * mm});
            skPoint(sketch, "E108", {"position": v(152.91, -83.62) * mm});
            skSolve(sketch);
        }
        {
            var Q0;
            Q0=sQuery(id+"F86.wireOp",VERTEX,"E107");
            var Q1;
            Q1=sQuery(id+"F86.wireOp",VERTEX,"E108");
            var Q2;
            Q2=sQuery(id+"F86.wireOp",VERTEX,"E106");
            var Q3;
            Q3=sQuery(id+"F86.wireOp",VERTEX,"E105");
            var Q4;
            Q4=makeQuery(id+"F12.opExtrude","SWEPT_BODY",BODY,{"disambiguationData":[OSD([sQuery(id+"F11.wireOp",EDGE,"E18.bottom"),sQuery(id+"F11.wireOp",EDGE,"E18.top"),sQuery(id+"F11.wireOp",EDGE,"E18.left"),sQuery(id+"F11.wireOp",EDGE,"E18.right"),sQuery(id+"F11.wireOp",EDGE,"E20.filletArc")])]});
            var Q5;
            Q5=makeQuery(id+"F80.opExtrude","SWEPT_BODY",BODY,{"disambiguationData":[OSD([sQuery(id+"F79.wireOp",EDGE,"E94.bottom"),sQuery(id+"F79.wireOp",EDGE,"E94.top"),sQuery(id+"F79.wireOp",EDGE,"E94.left"),sQuery(id+"F79.wireOp",EDGE,"E94.right"),sQuery(id+"F79.wireOp",EDGE,"E95.filletArc")])]});
            hole(context, id + "F87", {"style" : HoleStyle.SIMPLE, "endStyle" : HoleEndStyle.BLIND, "holeDiameter" : 3 * mm, "holeDepth" : 40 * mm, "tappedDepth" : 12 * mm, "tapClearance" : 3, "locations" : qUnion([Q0, Q1, Q2, Q3]), "scope" : qUnion([Q4, Q5])});
        }
        {
            var Q0;
            Q0=makeQuery(id+"F82.opExtrude","SWEPT_FACE",FACE,{"disambiguationData":[OSD([sQuery(id+"F81.wireOp",EDGE,"E100")])]});
            var sketch = newSketch(context, id + "F88", { "sketchPlane" : qUnion([Q0])});
            skPoint(sketch, "E109", {"position": v(-152.91, -98.62) * mm});
            skPoint(sketch, "E110", {"position": v(-152.91, -83.62) * mm});
            skPoint(sketch, "E111", {"position": v(-71.66, -98.62) * mm});
            skPoint(sketch, "E112", {"position": v(-71.66, -83.62) * mm});
            skSolve(sketch);
        }
        {
            var Q0;
            Q0=sQuery(id+"F88.wireOp",VERTEX,"E109");
            var Q1;
            Q1=sQuery(id+"F88.wireOp",VERTEX,"E110");
            var Q2;
            Q2=sQuery(id+"F88.wireOp",VERTEX,"E112");
            var Q3;
            Q3=sQuery(id+"F88.wireOp",VERTEX,"E111");
            var Q4;
            Q4=makeQuery(id+"F80.opExtrude","SWEPT_BODY",BODY,{"disambiguationData":[OSD([sQuery(id+"F79.wireOp",EDGE,"E94.bottom"),sQuery(id+"F79.wireOp",EDGE,"E94.top"),sQuery(id+"F79.wireOp",EDGE,"E94.left"),sQuery(id+"F79.wireOp",EDGE,"E94.right"),sQuery(id+"F79.wireOp",EDGE,"E95.filletArc")])]});
            hole(context, id + "F89", {"style" : HoleStyle.SIMPLE, "endStyle" : HoleEndStyle.BLIND, "oppositeDirection" : true, "holeDiameter" : 8 * mm, "holeDepth" : 80 * mm, "tappedDepth" : 12 * mm, "tapClearance" : 3, "startFromSketch" : true, "locations" : qUnion([Q0, Q1, Q2, Q3]), "scope" : qUnion([Q4])});
        }
        {
            var Q0;
            Q0=makeQuery(id+"F82.opExtrude","SWEPT_FACE",FACE,{"disambiguationData":[OSD([sQuery(id+"F81.wireOp",EDGE,"E99")])]});
            var sketch = newSketch(context, id + "F90", { "sketchPlane" : qUnion([Q0])});
            skPoint(sketch, "E113", {"position": v(61.11, -62.89) * mm});
            skPoint(sketch, "E114", {"position": v(164.13, -62.88) * mm});
            skPoint(sketch, "E115", {"position": v(90.08, -62.89) * mm});
            skPoint(sketch, "E116", {"position": v(128.1, -62.88) * mm});
            skSolve(sketch);
        }
        {
            var Q0;
            Q0=sQuery(id+"F90.wireOp",VERTEX,"E113");
            var Q1;
            Q1=sQuery(id+"F90.wireOp",VERTEX,"E115");
            var Q2;
            Q2=sQuery(id+"F90.wireOp",VERTEX,"E116");
            var Q3;
            Q3=sQuery(id+"F90.wireOp",VERTEX,"E114");
            var Q4;
            Q4=makeQuery(id+"F80.opExtrude","SWEPT_BODY",BODY,{"disambiguationData":[OSD([sQuery(id+"F79.wireOp",EDGE,"E94.bottom"),sQuery(id+"F79.wireOp",EDGE,"E94.top"),sQuery(id+"F79.wireOp",EDGE,"E94.left"),sQuery(id+"F79.wireOp",EDGE,"E94.right"),sQuery(id+"F79.wireOp",EDGE,"E95.filletArc")])]});
            hole(context, id + "F91", {"style" : HoleStyle.SIMPLE, "endStyle" : HoleEndStyle.BLIND, "holeDiameter" : 3 * mm, "holeDepth" : 10 * mm, "tappedDepth" : 12 * mm, "tapClearance" : 3, "locations" : qUnion([Q0, Q1, Q2, Q3]), "scope" : qUnion([Q4])});
        }
        {
            var Q0;
            Q0=makeQuery(id+"F12.opExtrude","CAP_FACE",FACE,{"disambiguationData":[OSD([sQuery(id+"F11.wireOp",EDGE,"E18.bottom"),sQuery(id+"F11.wireOp",EDGE,"E18.top"),sQuery(id+"F11.wireOp",EDGE,"E18.left"),sQuery(id+"F11.wireOp",EDGE,"E18.right"),sQuery(id+"F11.wireOp",EDGE,"E20.filletArc")])],"isStart":true});
            var sketch = newSketch(context, id + "F92", { "sketchPlane" : qUnion([Q0])});
            skPoint(sketch, "E117", {"position": v(61.11, -62.89) * mm});
            skPoint(sketch, "E118", {"position": v(90.08, -62.89) * mm});
            skPoint(sketch, "E119", {"position": v(128.1, -62.88) * mm});
            skPoint(sketch, "E120", {"position": v(164.13, -62.88) * mm});
            skSolve(sketch);
        }
        {
            var Q0;
            Q0=sQuery(id+"F92.wireOp",VERTEX,"E117");
            var Q1;
            Q1=sQuery(id+"F92.wireOp",VERTEX,"E118");
            var Q2;
            Q2=sQuery(id+"F92.wireOp",VERTEX,"E119");
            var Q3;
            Q3=sQuery(id+"F92.wireOp",VERTEX,"E120");
            var Q4;
            Q4=makeQuery(id+"F12.opExtrude","SWEPT_BODY",BODY,{"disambiguationData":[OSD([sQuery(id+"F11.wireOp",EDGE,"E18.bottom"),sQuery(id+"F11.wireOp",EDGE,"E18.top"),sQuery(id+"F11.wireOp",EDGE,"E18.left"),sQuery(id+"F11.wireOp",EDGE,"E18.right"),sQuery(id+"F11.wireOp",EDGE,"E20.filletArc")])]});
            hole(context, id + "F93", {"style" : HoleStyle.SIMPLE, "endStyle" : HoleEndStyle.BLIND, "holeDiameter" : 2.4 * mm, "holeDepth" : 15 * mm, "tappedDepth" : 12 * mm, "tapClearance" : 3, "locations" : qUnion([Q0, Q1, Q2, Q3]), "scope" : qUnion([Q4])});
        }
        {
            var Q0;
            Q0=makeQuery(id+"F12.opExtrude","SWEPT_BODY",BODY,{"disambiguationData":[OSD([sQuery(id+"F11.wireOp",EDGE,"E18.bottom"),sQuery(id+"F11.wireOp",EDGE,"E18.top"),sQuery(id+"F11.wireOp",EDGE,"E18.left"),sQuery(id+"F11.wireOp",EDGE,"E18.right"),sQuery(id+"F11.wireOp",EDGE,"E20.filletArc")])]});
            var Q1;
            Q1=qCreatedBy(makeId("Right.planeOp"),FACE);
            mirror(context, id + "F94", {"entities" : qUnion([Q0]), "mirrorPlane" : qUnion([Q1])});
        }
        {
            var Q0;
            Q0=makeQuery(id+"F80.opExtrude","SWEPT_BODY",BODY,{"disambiguationData":[OSD([sQuery(id+"F79.wireOp",EDGE,"E94.bottom"),sQuery(id+"F79.wireOp",EDGE,"E94.top"),sQuery(id+"F79.wireOp",EDGE,"E94.left"),sQuery(id+"F79.wireOp",EDGE,"E94.right"),sQuery(id+"F79.wireOp",EDGE,"E95.filletArc")])]});
            var Q1;
            Q1=qCreatedBy(makeId("Right.planeOp"),FACE);
            mirror(context, id + "F95", {"entities" : qUnion([Q0]), "mirrorPlane" : qUnion([Q1])});
        }
        {
            var Q0;
            Q0=makeQuery(id+"F1.opExtrude","SWEPT_BODY",BODY,{"disambiguationData":[OSD([sQuery(id+"F0.wireOp",EDGE,"E0.bottom"),sQuery(id+"F0.wireOp",EDGE,"E0.top"),sQuery(id+"F0.wireOp",EDGE,"E0.left"),sQuery(id+"F0.wireOp",EDGE,"E0.right"),sQuery(id+"F0.wireOp",EDGE,"E3.filletArc")])]});
            var Q1;
            Q1=qCreatedBy(makeId("Right.planeOp"),FACE);
            mirror(context, id + "F96", {"entities" : qUnion([Q0]), "mirrorPlane" : qUnion([Q1])});
        }
        {
            var Q0;
            Q0=makeQuery(id+"F43.opExtrude","SWEPT_BODY",BODY,{"disambiguationData":[OSD([sQuery(id+"F42.wireOp",EDGE,"E49.bottom"),sQuery(id+"F42.wireOp",EDGE,"E49.top"),sQuery(id+"F42.wireOp",EDGE,"E49.left"),sQuery(id+"F42.wireOp",EDGE,"E49.right"),sQuery(id+"F42.wireOp",EDGE,"E50"),sQuery(id+"F42.wireOp",EDGE,"E51")])]});
            var Q1;
            Q1=qCreatedBy(makeId("Right.planeOp"),FACE);
            mirror(context, id + "F97", {"entities" : qUnion([Q0]), "mirrorPlane" : qUnion([Q1])});
        }
        {
            var Q0;
            Q0=makeQuery(id+"F40.opExtrude","SWEPT_BODY",BODY,{"disambiguationData":[OSD([sQuery(id+"F39.wireOp",EDGE,"E43.bottom"),sQuery(id+"F39.wireOp",EDGE,"E43.top"),sQuery(id+"F39.wireOp",EDGE,"E43.left"),sQuery(id+"F39.wireOp",EDGE,"E43.right"),sQuery(id+"F39.wireOp",EDGE,"E47"),sQuery(id+"F39.wireOp",EDGE,"E48")])]});
            var Q1;
            Q1=qCreatedBy(makeId("Right.planeOp"),FACE);
            mirror(context, id + "F98", {"entities" : qUnion([Q0]), "mirrorPlane" : qUnion([Q1])});
        }
    });
